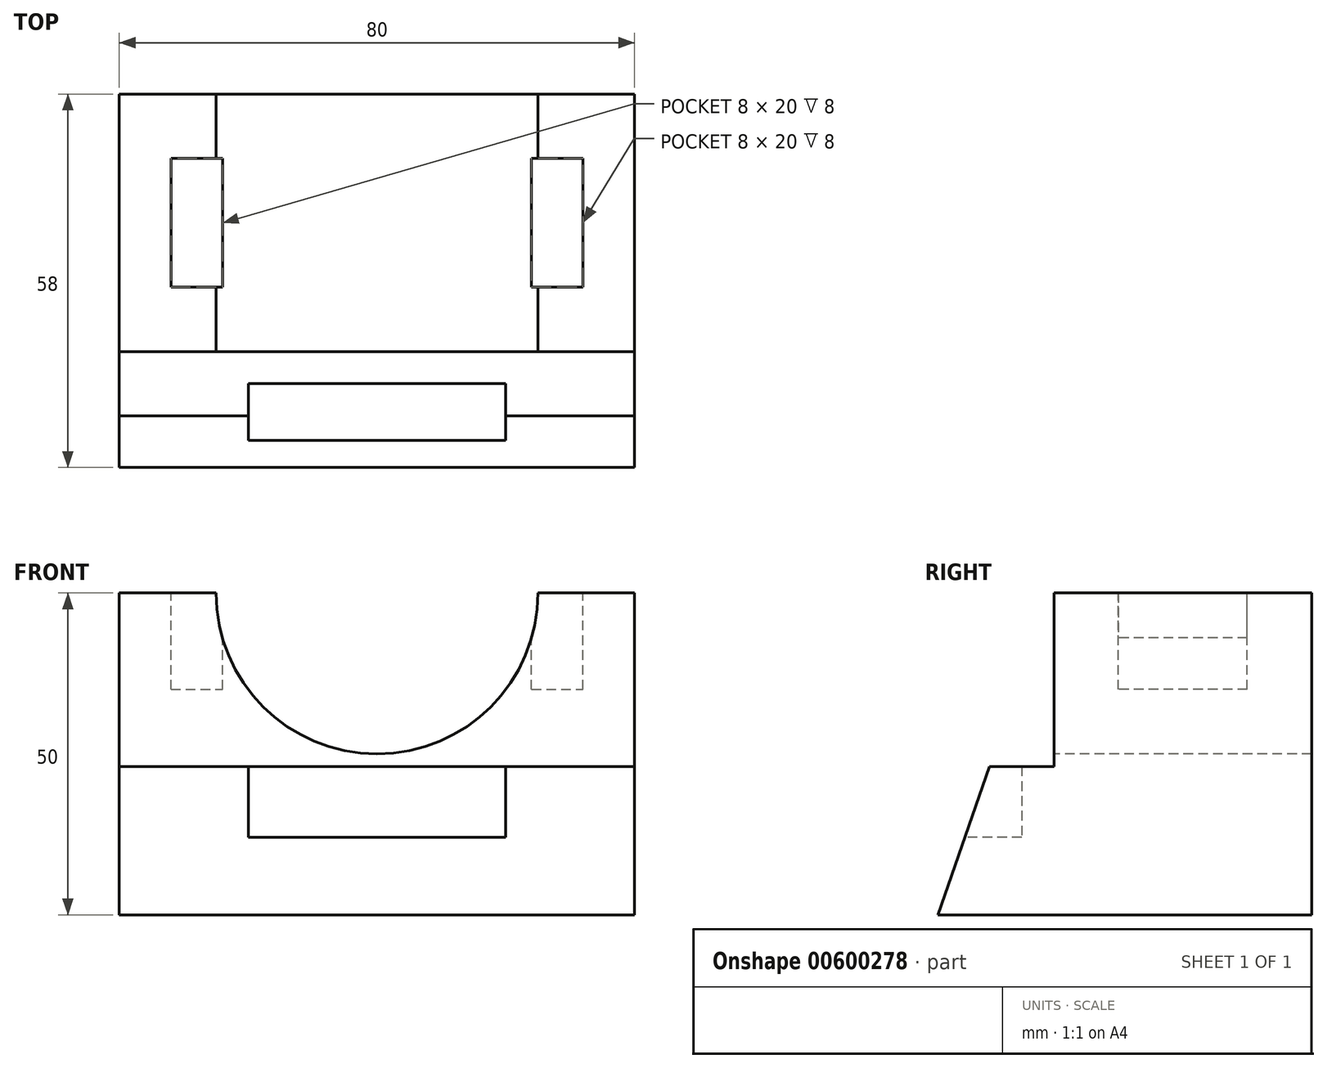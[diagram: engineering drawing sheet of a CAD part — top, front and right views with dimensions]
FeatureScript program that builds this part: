
annotation { "Feature Type Name" : "Feature", "Feature Type Description" : "" }
export const myFeature = defineFeature(function(context is Context, id is Id, definition is map)
    precondition{}
    {
        {
            var Q0;
            Q0=qCreatedBy(makeId("Top.planeOp"),FACE);
            var sketch = newSketch(context, id + "F0", { "sketchPlane" : qUnion([Q0])});
            skLineSegment(sketch, "E0.bottom", {"start": v(40, 29) * mm, "end": v(-40, 29) * mm});
            skLineSegment(sketch, "E0.top", {"start": v(40, -29) * mm, "end": v(-40, -29) * mm});
            skLineSegment(sketch, "E0.left", {"start": v(40, 29) * mm, "end": v(40, -29) * mm});
            skLineSegment(sketch, "E0.right", {"start": v(-40, 29) * mm, "end": v(-40, -29) * mm});
            skPoint(sketch, "E0.middle", {"position": v(0, 0) * mm});
            skSolve(sketch);
        }
        {
            var Q0;
            Q0=makeQuery(id+"F0.imprint","IMPRINT",FACE,{"disambiguationData":[TD([[makeQuery(id+"F0.imprint","IMPRINT",EDGE,{"derivedFrom":sQuery(id+"F0.wireOp",EDGE,"E0.bottom")}),1.0]])]});
            extrude(context, id + "F1", {"entities" : qUnion([Q0]), "depth" : 50 * mm, "offsetDistance" : 25 * mm});
        }
        {
            var Q0;
            Q0=makeQuery(id+"F1.opExtrude","SWEPT_FACE",FACE,{"disambiguationData":[OSD([sQuery(id+"F0.wireOp",EDGE,"E0.right")])]});
            var sketch = newSketch(context, id + "F2", { "sketchPlane" : qUnion([Q0])});
            skLineSegment(sketch, "E1", {"start": v(-29, 50) * mm, "end": v(11, 50) * mm});
            skLineSegment(sketch, "E2", {"start": v(11, 50) * mm, "end": v(11, 23.05) * mm});
            skLineSegment(sketch, "E3", {"start": v(11, 23.05) * mm, "end": v(21, 23.05) * mm});
            skLineSegment(sketch, "E4", {"start": v(21, 23.05) * mm, "end": v(29, 0) * mm});
            skLineSegment(sketch, "E5", {"start": v(29, 0) * mm, "end": v(-29, 0) * mm});
            skLineSegment(sketch, "E6", {"start": v(-29, 0) * mm, "end": v(-29, 50) * mm});
            skSolve(sketch);
        }
        {
            var Q0;
            {var subQ2=sQuery(id+"F2.wireOp",EDGE,"E2");Q0=makeQuery(id+"F2.imprint","IMPRINT",FACE,{"disambiguationData":[TD([[makeQuery(id+"F2.imprint","IMPRINT",EDGE,{"derivedFrom":subQ2}),1.0]])]});}
            extrude(context, id + "F3", {"entities" : qUnion([Q0]), "operationType" : NewBodyOperationType.REMOVE, "endBound" : BoundingType.THROUGH_ALL, "oppositeDirection" : true, "depth" : 25 * mm, "offsetDistance" : 25 * mm});
        }
        {
            var Q0;
            Q0=makeQuery(id+"F1.opExtrude","SWEPT_FACE",FACE,{"disambiguationData":[OSD([sQuery(id+"F0.wireOp",EDGE,"E0.right")])]});
            cPlane(context, id + "F4", {"entities" : qUnion([Q0]), "cplaneType" : CPlaneType.OFFSET, "offset" : 20 * mm, "oppositeDirection" : true, "width" : 150 * mm, "height" : 150 * mm});
        }
        {
            var Q0;
            Q0=qCreatedBy(id+"F4.planeOp",FACE);
            var sketch = newSketch(context, id + "F5", { "sketchPlane" : qUnion([Q0])});
            skLineSegment(sketch, "E7", {"start": v(21, 23.05) * mm, "end": v(16, 23.05) * mm});
            skLineSegment(sketch, "E8", {"start": v(16, 23.05) * mm, "end": v(16, 12.05) * mm});
            skLineSegment(sketch, "E9", {"start": v(16, 12.05) * mm, "end": v(24.82, 12.05) * mm});
            skLineSegment(sketch, "E10", {"start": v(21, 23.05) * mm, "end": v(24.82, 12.05) * mm});
            skSolve(sketch);
        }
        {
            var Q0;
            Q0 = qSketchRegion(id + "F5", true);
            extrude(context, id + "F6", {"entities" : qUnion([Q0]), "operationType" : NewBodyOperationType.REMOVE, "oppositeDirection" : true, "depth" : 40 * mm, "offsetDistance" : 25 * mm});
        }
        {
            var Q0;
            Q0=makeQuery(id+"F1.opExtrude","CAP_FACE",FACE,{"disambiguationData":[OSD([sQuery(id+"F0.wireOp",EDGE,"E0.bottom"),sQuery(id+"F0.wireOp",EDGE,"E0.top"),sQuery(id+"F0.wireOp",EDGE,"E0.left"),sQuery(id+"F0.wireOp",EDGE,"E0.right")])],"isStart":false});
            var sketch = newSketch(context, id + "F7", { "sketchPlane" : qUnion([Q0])});
            skLineSegment(sketch, "E11", {"start": v(0, 29) * mm, "end": v(0, -11) * mm, "construction": true});
            skLineSegment(sketch, "E12", {"start": v(-24, 29) * mm, "end": v(-24, 19) * mm});
            skLineSegment(sketch, "E13", {"start": v(-24, 19) * mm, "end": v(-32, 19) * mm});
            skLineSegment(sketch, "E14", {"start": v(-32, 19) * mm, "end": v(-32, -1) * mm});
            skLineSegment(sketch, "E15", {"start": v(-32, -1) * mm, "end": v(-24, -1) * mm});
            skLineSegment(sketch, "E16", {"start": v(-24, -1) * mm, "end": v(-24, -11) * mm});
            skLineSegment(sketch, "E17", {"start": v(-24, 19) * mm, "end": v(-24, -1) * mm});
            skLineSegment(sketch, "E18.MirrorCS", {"start": v(24, 19) * mm, "end": v(24, -1) * mm});
            skLineSegment(sketch, "E19.MirrorCS", {"start": v(24, 19) * mm, "end": v(32, 19) * mm});
            skLineSegment(sketch, "E20.MirrorCS", {"start": v(32, 19) * mm, "end": v(32, -1) * mm});
            skLineSegment(sketch, "E21.MirrorCS", {"start": v(32, -1) * mm, "end": v(24, -1) * mm});
            skSolve(sketch);
        }
        {
            var Q0;
            Q0 = qSketchRegion(id + "F7", true);
            extrude(context, id + "F8", {"entities" : qUnion([Q0]), "operationType" : NewBodyOperationType.REMOVE, "oppositeDirection" : true, "depth" : 15 * mm, "offsetDistance" : 25 * mm});
        }
        {
            var Q0;
            Q0=makeQuery(id+"F3.boolean.opBoolean","COPY",FACE,{"derivedFrom":makeQuery(id+"F3.opExtrude","SWEPT_FACE",FACE,{"disambiguationData":[OSD([sQuery(id+"F2.wireOp",EDGE,"E2")])]})});
            var sketch = newSketch(context, id + "F9", { "sketchPlane" : qUnion([Q0])});
            skLineSegment(sketch, "E22", {"start": v(0, 50) * mm, "end": v(0, 23.05) * mm, "construction": true});
            skArc(sketch, "E23", {"start": v(-25, 50) * mm, "mid": v(0, 25) * mm, "end": v(25, 50) * mm});
            skSolve(sketch);
        }
        {
            var Q0;
            {var subQ0=sQuery(id+"F9.wireOp",EDGE,"E23");Q0=makeQuery(id+"F9.imprint","IMPRINT",FACE,{"disambiguationData":[TD([[makeQuery(id+"F9.imprint","IMPRINT",EDGE,{"derivedFrom":subQ0}),1.0]])]});}
            extrude(context, id + "F10", {"entities" : qUnion([Q0]), "operationType" : NewBodyOperationType.REMOVE, "endBound" : BoundingType.THROUGH_ALL, "oppositeDirection" : true, "depth" : 25 * mm, "offsetDistance" : 25 * mm});
        }
    });
